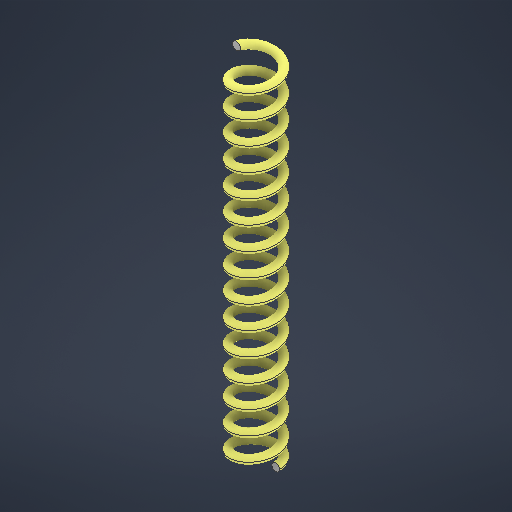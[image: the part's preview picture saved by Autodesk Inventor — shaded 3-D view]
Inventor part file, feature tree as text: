
AUTODESK INVENTOR PART (.ipt)
format: ipt  version: 2025.2 (Build 292293000, 293)  size: 720,896 bytes
history: native  units: mm
features: helix x1, sketch x1
ambient origin geometry x8: Origin, YZ Plane, XZ Plane, XY Plane, X Axis, Y Axis, Z Axis, Center Point
bodies: Solid1 (feature_tree)
feature tree (2):
  helix  "Coil1"  [1 undecoded]
  sketch  "Sketch2"  dims[d1=5.0mm d2=2.0mm d3=5.8mm d4=10.0mm d5=150.0mm d6=0.0mm d7=90.0deg d8=90.0deg d9=0.0mm d10=0.0mm]
note: 1 required parameter value undecoded (feature->parameter linkage not recoverable at this tier; creation-order binding heuristic only, values carry confidence <= 0.55)
